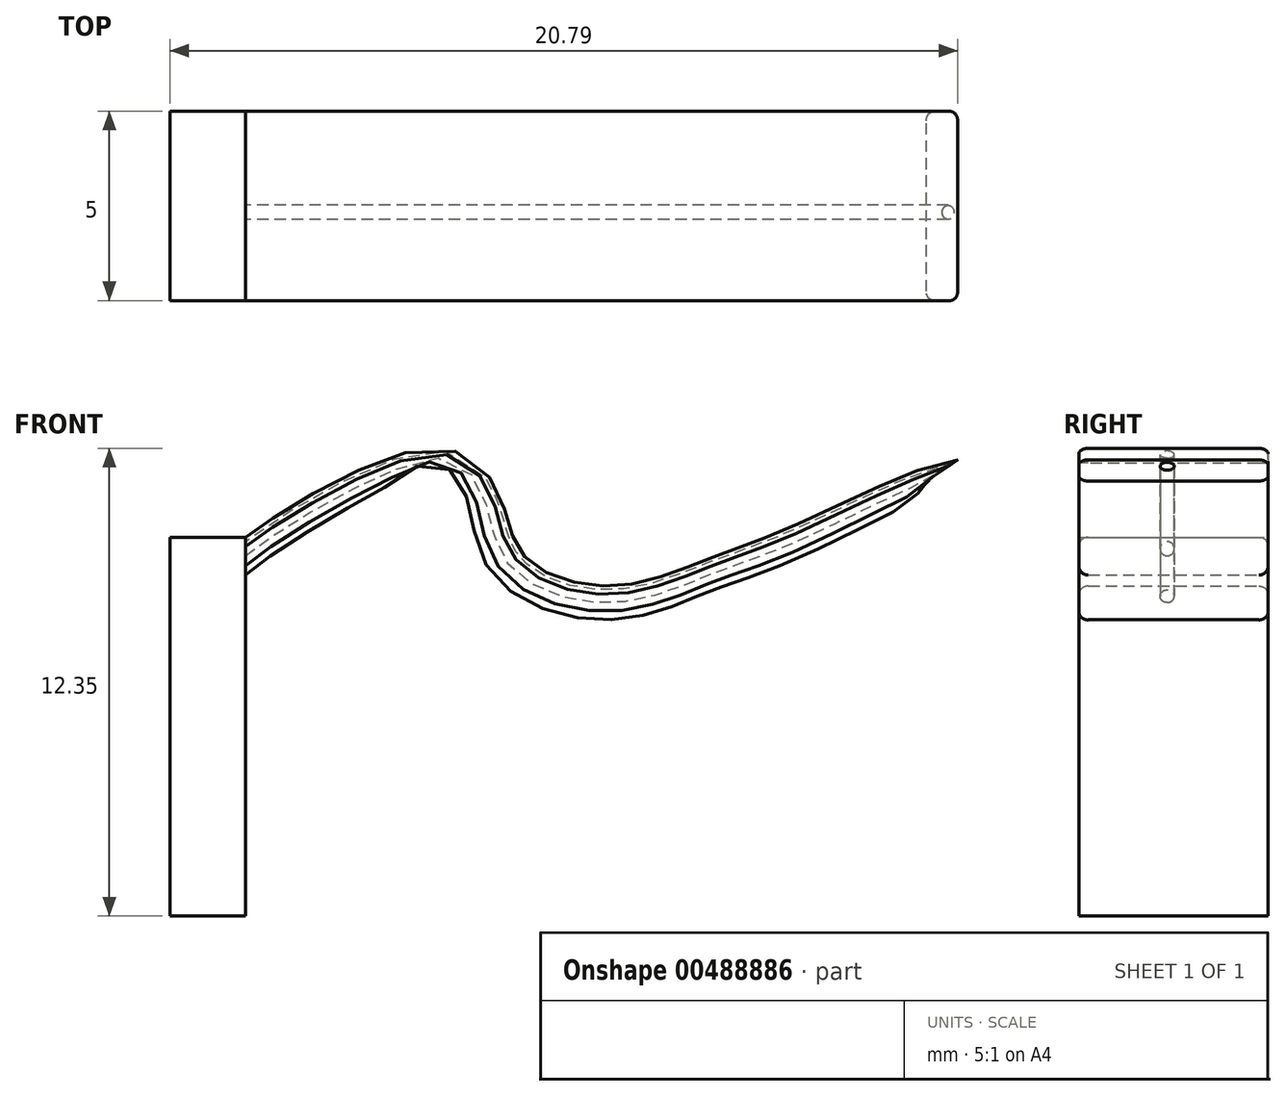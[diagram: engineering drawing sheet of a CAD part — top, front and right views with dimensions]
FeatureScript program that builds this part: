
annotation { "Feature Type Name" : "Feature", "Feature Type Description" : "" }
export const myFeature = defineFeature(function(context is Context, id is Id, definition is map)
    precondition{}
    {
        {
            var Q0;
            Q0=qCreatedBy(makeId("Right.planeOp"),FACE);
            var sketch = newSketch(context, id + "F0", { "sketchPlane" : qUnion([Q0])});
            skLineSegment(sketch, "E0.bottom", {"start": v(-2.33, 10) * mm, "end": v(2.67, 10) * mm});
            skLineSegment(sketch, "E0.top", {"start": v(-2.33, 0) * mm, "end": v(2.67, 0) * mm});
            skLineSegment(sketch, "E0.left", {"start": v(-2.33, 10) * mm, "end": v(-2.33, 0) * mm});
            skLineSegment(sketch, "E0.right", {"start": v(2.67, 10) * mm, "end": v(2.67, 0) * mm});
            skSolve(sketch);
        }
        {
            var Q0;
            Q0 = qSketchRegion(id + "F0", true);
            var Q1;
            Q1=makeQuery(id+"F0.imprint","IMPRINT",FACE,{"disambiguationData":[TD([[makeQuery(id+"F0.imprint","IMPRINT",EDGE,{"derivedFrom":sQuery(id+"F0.wireOp",EDGE,"E0.bottom")}),-1.0]])]});
            extrude(context, id + "F1", {"entities" : qUnion([Q0, Q1]), "depth" : 2 * mm});
        }
        {
            var Q0;
            Q0=makeQuery(id+"F1.opExtrude","CAP_FACE",FACE,{"disambiguationData":[OSD([sQuery(id+"F0.wireOp",EDGE,"E0.bottom"),sQuery(id+"F0.wireOp",EDGE,"E0.top"),sQuery(id+"F0.wireOp",EDGE,"E0.left"),sQuery(id+"F0.wireOp",EDGE,"E0.right")])],"isStart":false});
            cPlane(context, id + "F2", {"entities" : qUnion([Q0]), "cplaneType" : CPlaneType.OFFSET, "offset" : 0 * mm, "width" : 150 * mm, "height" : 150 * mm});
        }
        {
            var Q0;
            Q0=qCreatedBy(id+"F2.planeOp",FACE);
            var sketch = newSketch(context, id + "F3", { "sketchPlane" : qUnion([Q0])});
            skLineSegment(sketch, "E1.bottom", {"start": v(-2.08, 10) * mm, "end": v(2.42, 10) * mm});
            skLineSegment(sketch, "E1.top", {"start": v(-2.08, 9) * mm, "end": v(2.42, 9) * mm});
            skLineSegment(sketch, "E1.left", {"start": v(-2.33, 9.75) * mm, "end": v(-2.33, 9.25) * mm});
            skLineSegment(sketch, "E1.right", {"start": v(2.67, 9.75) * mm, "end": v(2.67, 9.25) * mm});
            skPoint(sketch, "E2.visualSharp", {"position": v(-2.33, 10) * mm});
            skArc(sketch, "E2.filletArc", {"start": v(-2.08, 10) * mm, "mid": v(-2.26, 9.93) * mm, "end": v(-2.33, 9.75) * mm});
            skPoint(sketch, "E3.visualSharp", {"position": v(-2.33, 9) * mm});
            skArc(sketch, "E3.filletArc", {"start": v(-2.33, 9.25) * mm, "mid": v(-2.26, 9.07) * mm, "end": v(-2.08, 9) * mm});
            skPoint(sketch, "E4.visualSharp", {"position": v(2.67, 9) * mm});
            skArc(sketch, "E4.filletArc", {"start": v(2.42, 9) * mm, "mid": v(2.6, 9.07) * mm, "end": v(2.67, 9.25) * mm});
            skPoint(sketch, "E5.visualSharp", {"position": v(2.67, 10) * mm});
            skArc(sketch, "E5.filletArc", {"start": v(2.67, 9.75) * mm, "mid": v(2.6, 9.93) * mm, "end": v(2.42, 10) * mm});
            skCircle(sketch, "E6", {"center": v(0, 9.7) * mm, "radius": 0.19 * mm});
            skLineSegment(sketch, "E7", {"start": v(-2.08, 10) * mm, "end": v(0, 9.89) * mm});
            skLineSegment(sketch, "E8", {"start": v(0, 9.89) * mm, "end": v(2.42, 10) * mm});
            skSolve(sketch);
        }
        {
            var Q0;
            Q0=makeQuery(id+"F1.opExtrude","SWEPT_FACE",FACE,{"disambiguationData":[OSD([sQuery(id+"F0.wireOp",EDGE,"E0.left")])]});
            cPlane(context, id + "F4", {"entities" : qUnion([Q0]), "cplaneType" : CPlaneType.OFFSET, "offset" : 0 * mm, "width" : 150 * mm, "height" : 150 * mm});
        }
        {
            var Q0;
            Q0=qCreatedBy(id+"F4.planeOp",FACE);
            var sketch = newSketch(context, id + "F5", { "sketchPlane" : qUnion([Q0])});
            skFitSpline(sketch, "E9", {"points": [v(2.8, 9.67) * mm, v(7.24, 11.54) * mm, v(8.72, 9.23) * mm, v(11.78, 8.01) * mm, v(14.6, 8.8) * mm, v(17.05, 9.77) * mm, v(20.96, 11.2) * mm], "startDerivative": vector(10.62, 7.53) * mm, "endDerivative": vector(9.42, -3.56) * mm});
            skSolve(sketch);
        }
        {
            var Q0;
            Q0=makeQuery(id+"F3.imprint","IMPRINT",FACE,{"disambiguationData":[TD([[makeQuery(id+"F3.imprint","IMPRINT",EDGE,{"derivedFrom":sQuery(id+"F3.wireOp",EDGE,"E1.bottom")}),-1.0]])]});
            var Q1;
            Q1=makeQuery(id+"F3.imprint","IMPRINT",FACE,{"disambiguationData":[TD([[makeQuery(id+"F3.imprint","IMPRINT",EDGE,{"derivedFrom":sQuery(id+"F3.wireOp",EDGE,"E1.top")}),1.0]])]});
            var Q2;
            Q2=sQuery(id+"F5.wireOp",EDGE,"E9");
            sweep(context, id + "F6", {"profiles" : qUnion([Q0, Q1]), "path" : qUnion([Q2])});
        }
    });
